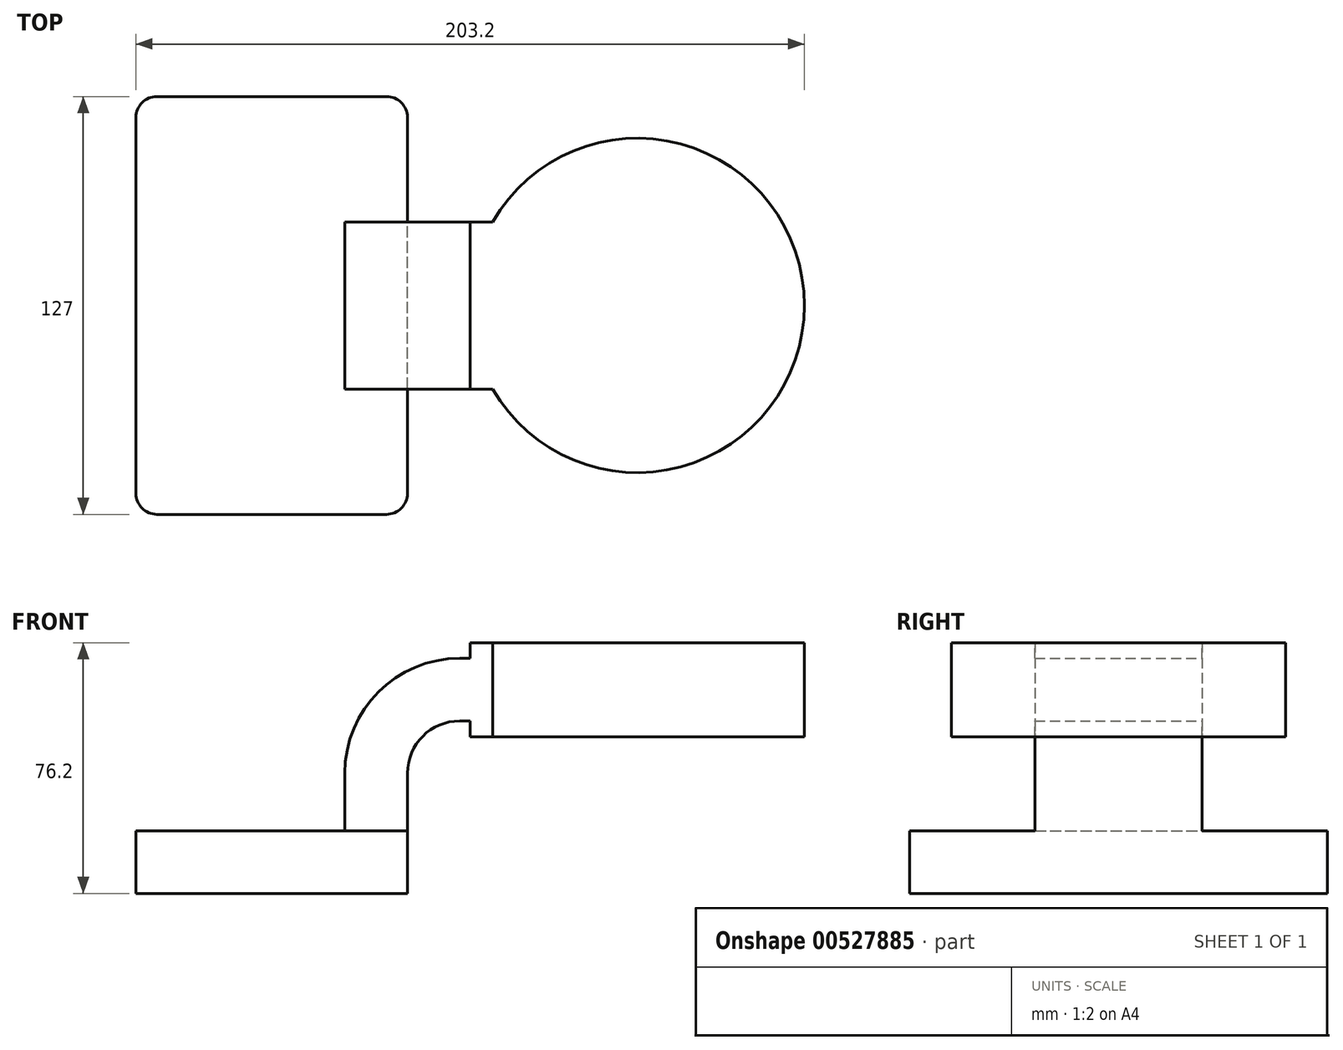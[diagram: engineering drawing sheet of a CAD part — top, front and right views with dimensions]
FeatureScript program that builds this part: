
annotation { "Feature Type Name" : "Feature", "Feature Type Description" : "" }
export const myFeature = defineFeature(function(context is Context, id is Id, definition is map)
    precondition{}
    {
        {
            var Q0;
            Q0=qCreatedBy(makeId("Front.planeOp"),FACE);
            var sketch = newSketch(context, id + "F0", { "sketchPlane" : qUnion([Q0])});
            skLineSegment(sketch, "E0.bottom", {"start": v(-41.28, -9.53) * mm, "end": v(41.28, -9.53) * mm});
            skLineSegment(sketch, "E0.top", {"start": v(-41.28, 9.53) * mm, "end": v(41.28, 9.53) * mm});
            skLineSegment(sketch, "E0.left", {"start": v(-41.28, -9.53) * mm, "end": v(-41.28, 9.53) * mm});
            skLineSegment(sketch, "E0.right", {"start": v(41.28, -9.53) * mm, "end": v(41.28, 9.53) * mm});
            skPoint(sketch, "E0.middle", {"position": v(0, 0) * mm});
            skLineSegment(sketch, "E1.bottom", {"start": v(60.32, 38.1) * mm, "end": v(111.12, 38.1) * mm});
            skLineSegment(sketch, "E1.top", {"start": v(60.32, 66.67) * mm, "end": v(111.12, 66.67) * mm});
            skLineSegment(sketch, "E1.left", {"start": v(60.32, 38.1) * mm, "end": v(60.32, 66.67) * mm});
            skLineSegment(sketch, "E1.right", {"start": v(111.12, 38.1) * mm, "end": v(111.12, 66.67) * mm});
            skPoint(sketch, "E1.middle", {"position": v(85.72, 52.39) * mm});
            skLineSegment(sketch, "E2", {"start": v(41.27, 9.53) * mm, "end": v(41.27, 27) * mm});
            skArc(sketch, "E3", {"start": v(41.27, 27) * mm, "mid": v(45.92, 38.23) * mm, "end": v(57.15, 42.88) * mm});
            skLineSegment(sketch, "E4", {"start": v(57.15, 42.88) * mm, "end": v(87.13, 42.88) * mm});
            skLineSegment(sketch, "E5.0", {"start": v(57.15, 61.93) * mm, "end": v(87.13, 61.93) * mm});
            skArc(sketch, "E5.1", {"start": v(22.23, 27) * mm, "mid": v(32.45, 51.7) * mm, "end": v(57.15, 61.93) * mm});
            skLineSegment(sketch, "E5.2", {"start": v(22.22, 9.53) * mm, "end": v(22.22, 27) * mm});
            skFitSpline(sketch, "E6", {"points": [v(-41.28, 9.53) * mm, v(57.15, 61.93) * mm], "startDerivative": vector(60.23, 132.73) * mm, "endDerivative": vector(119.7, -23.17) * mm});
            skSolve(sketch);
        }
        {
            var Q0;
            Q0=makeQuery(id+"F0.imprint","IMPRINT",FACE,{"disambiguationData":[TD([[makeQuery(id+"F0.imprint","IMPRINT",EDGE,{"derivedFrom":sQuery(id+"F0.wireOp",EDGE,"E0.bottom")}),1.0]])]});
            extrude(context, id + "F1", {"entities" : qUnion([Q0]), "endBound" : BoundingType.SYMMETRIC, "depth" : 127 * mm, "offsetDistance" : 25.4 * mm});
        }
        {
            var Q0;
            {var subQ0=sQuery(id+"F0.wireOp",EDGE,"E2");Q0=makeQuery(id+"F0.imprint","IMPRINT",FACE,{"disambiguationData":[TD([[makeQuery(id+"F0.imprint","IMPRINT",EDGE,{"derivedFrom":subQ0}),1.0]])]});}
            var Q1;
            {var subQ3=sQuery(id+"F0.wireOp",EDGE,"E1.bottom");Q1=makeQuery(id+"F0.imprint","IMPRINT",FACE,{"disambiguationData":[TD([[makeQuery(id+"F0.imprint","IMPRINT",EDGE,{"derivedFrom":subQ3}),1.0]])]});}
            extrude(context, id + "F2", {"entities" : qUnion([Q0, Q1]), "operationType" : NewBodyOperationType.ADD, "endBound" : BoundingType.SYMMETRIC, "depth" : 50.8 * mm, "offsetDistance" : 25.4 * mm});
        }
        {
            var Q0;
            Q0=makeQuery(id+"F0.imprint","IMPRINT",FACE,{"disambiguationData":[TD([[makeQuery(id+"F0.imprint","IMPRINT",EDGE,{"derivedFrom":sQuery(id+"F0.wireOp",EDGE,"E5.1")}),1.0]])]});
            extrude(context, id + "F3", {"entities" : qUnion([Q0]), "operationType" : NewBodyOperationType.ADD, "endBound" : BoundingType.SYMMETRIC, "depth" : 15.88 * mm, "offsetDistance" : 25.4 * mm});
        }
        {
            var Q0;
            {var subQ3=sQuery(id+"F0.wireOp",EDGE,"E1.bottom");Q0=makeQuery(id+"F0.imprint","IMPRINT",FACE,{"disambiguationData":[TD([[makeQuery(id+"F0.imprint","IMPRINT",EDGE,{"derivedFrom":subQ3}),1.0]])]});}
            var Q1;
            Q1=sQuery(id+"F0.wireOp",EDGE,"E1.right");
            revolve(context, id + "F4", {"operationType" : NewBodyOperationType.ADD, "entities" : qUnion([Q0]), "axis" : qUnion([Q1]), "revolveType" : RevolveType.FULL});
        }
        {
            var Q0;
            Q0=makeQuery(id+"F1.opExtrude","CAP_EDGE",EDGE,{"disambiguationData":[OSD([sQuery(id+"F0.wireOp",EDGE,"E0.left")])],"isStart":false});
            var Q1;
            Q1=makeQuery(id+"F1.opExtrude","CAP_EDGE",EDGE,{"disambiguationData":[OSD([sQuery(id+"F0.wireOp",EDGE,"E0.left")])],"isStart":true});
            var Q2;
            Q2=makeQuery(id+"F1.opExtrude","CAP_EDGE",EDGE,{"disambiguationData":[OSD([sQuery(id+"F0.wireOp",EDGE,"E0.right")])],"isStart":true});
            var Q3;
            Q3=makeQuery(id+"F1.opExtrude","CAP_EDGE",EDGE,{"disambiguationData":[OSD([sQuery(id+"F0.wireOp",EDGE,"E0.right")])],"isStart":false});
            fillet(context, id + "F5", {"entities" : qUnion([Q0, Q1, Q2, Q3]), "radius" : 6.35 * mm, "tangentPropagation" : true, "allowEdgeOverflow" : false});
        }
    });
